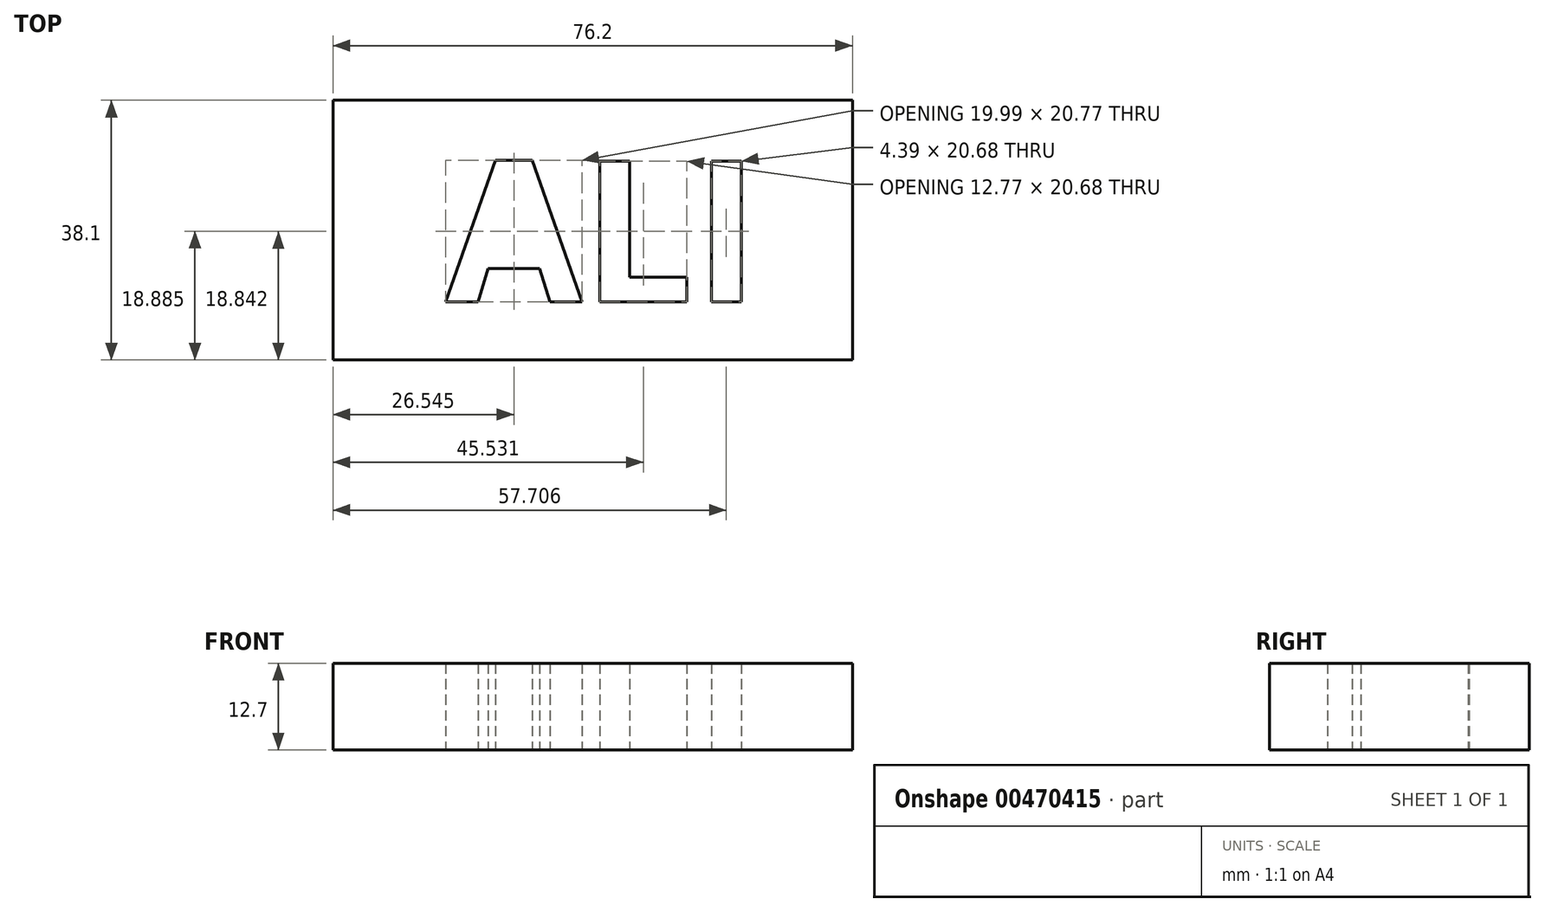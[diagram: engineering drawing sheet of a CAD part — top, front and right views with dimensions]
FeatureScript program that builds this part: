
annotation { "Feature Type Name" : "Feature", "Feature Type Description" : "" }
export const myFeature = defineFeature(function(context is Context, id is Id, definition is map)
    precondition{}
    {
        {
            var Q0;
            Q0=qCreatedBy(makeId("Top.planeOp"),FACE);
            var sketch = newSketch(context, id + "F0", { "sketchPlane" : qUnion([Q0])});
            skLineSegment(sketch, "E0.bottom", {"start": v(-38.1, 19.05) * mm, "end": v(38.1, 19.05) * mm});
            skLineSegment(sketch, "E0.top", {"start": v(-38.1, -19.05) * mm, "end": v(38.1, -19.05) * mm});
            skLineSegment(sketch, "E0.left", {"start": v(-38.1, 19.05) * mm, "end": v(-38.1, -19.05) * mm});
            skLineSegment(sketch, "E0.right", {"start": v(38.1, 19.05) * mm, "end": v(38.1, -19.05) * mm});
            skPoint(sketch, "E0.middle", {"position": v(0, 0) * mm});
            skText(sketch, "E1", { "text": "ALI", "fontName": "OpenSans-Bold.ttf"});
            const initialGuessF0  = {"E1": [-0.02155, -0.01055, 1, 0, 0.02086]};
            skSetInitialGuess(sketch, initialGuessF0);
            skSolve(sketch);
        }
        {
            var Q0;
            Q0 = qSketchRegion(id + "F0", true);
            extrude(context, id + "F1", {"entities" : qUnion([Q0]), "depth" : 12.7 * mm});
        }
    });
